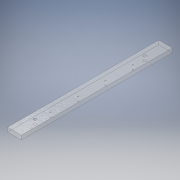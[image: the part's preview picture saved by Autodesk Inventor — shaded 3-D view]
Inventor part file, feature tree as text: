
AUTODESK INVENTOR PART (.ipt)
format: ipt  version: 2019 (Build 230136000, 136)  size: 126,976 bytes
history: native  units: mm
features: extrude x1, sketch x1
ambient origin geometry x8: Origin, YZ Plane, XZ Plane, XY Plane, X Axis, Y Axis, Z Axis, Center Point
bodies: Body1 (feature_tree)
feature tree (2):
  extrude  "Extrusion2"  Depth=20.0mm
  sketch  "Sketch2"  dims[d31=6.0mm d32=0.0mm d76=20.0mm d78=30.0mm d80=10.0mm d81=4.5mm d82=30.0mm d83=220.0mm d84=1.9mm d85=40.0mm d87=40.0mm d88=10.0mm d90=10.0mm d92=7.5mm d93=20.0mm]
